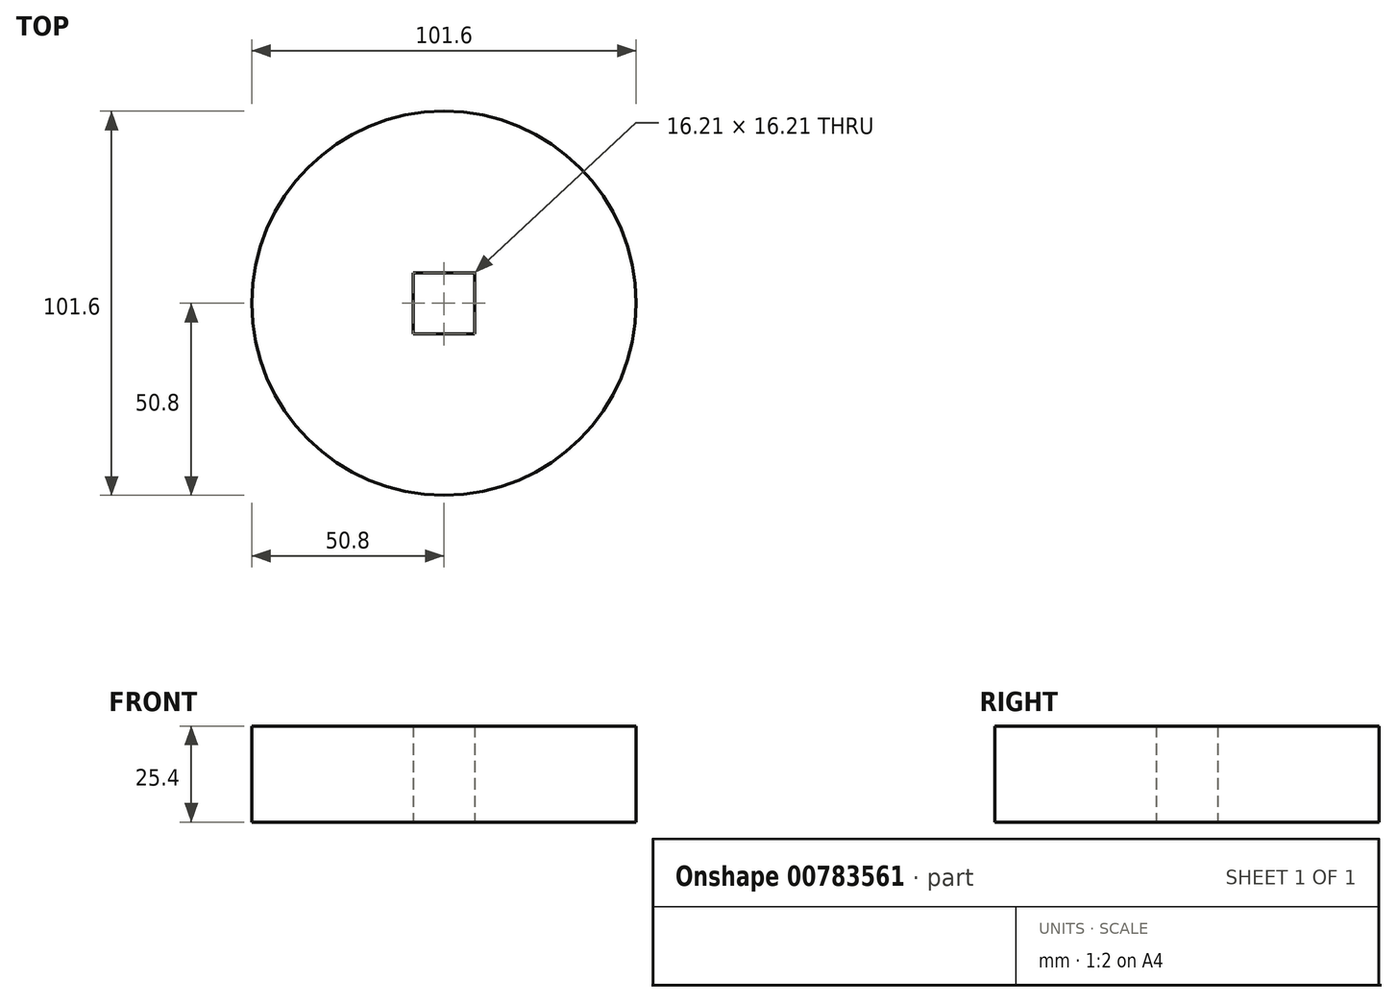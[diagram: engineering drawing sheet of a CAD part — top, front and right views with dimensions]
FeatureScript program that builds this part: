
annotation { "Feature Type Name" : "Feature", "Feature Type Description" : "" }
export const myFeature = defineFeature(function(context is Context, id is Id, definition is map)
    precondition{}
    {
        {
            var Q0;
            Q0=qCreatedBy(makeId("Top.planeOp"),FACE);
            var sketch = newSketch(context, id + "F0", { "sketchPlane" : qUnion([Q0])});
            skCircle(sketch, "E0", {"center": v(0, 0) * mm, "radius": 50.8 * mm});
            skLineSegment(sketch, "E1.bottom", {"start": v(8.1, -8.1) * mm, "end": v(-8.1, -8.1) * mm});
            skLineSegment(sketch, "E1.top", {"start": v(8.1, 8.1) * mm, "end": v(-8.1, 8.1) * mm});
            skLineSegment(sketch, "E1.left", {"start": v(8.1, -8.1) * mm, "end": v(8.1, 8.1) * mm});
            skLineSegment(sketch, "E1.right", {"start": v(-8.1, -8.1) * mm, "end": v(-8.1, 8.1) * mm});
            skSolve(sketch);
        }
        {
            var Q0;
            Q0=makeQuery(id+"F0.imprint","IMPRINT",FACE,{"disambiguationData":[TD([[makeQuery(id+"F0.imprint","IMPRINT",EDGE,{"derivedFrom":sQuery(id+"F0.wireOp",EDGE,"E0")}),1.0]])]});
            extrude(context, id + "F1", {"entities" : qUnion([Q0]), "depth" : 25.4 * mm, "offsetDistance" : 25.4 * mm});
        }
    });
